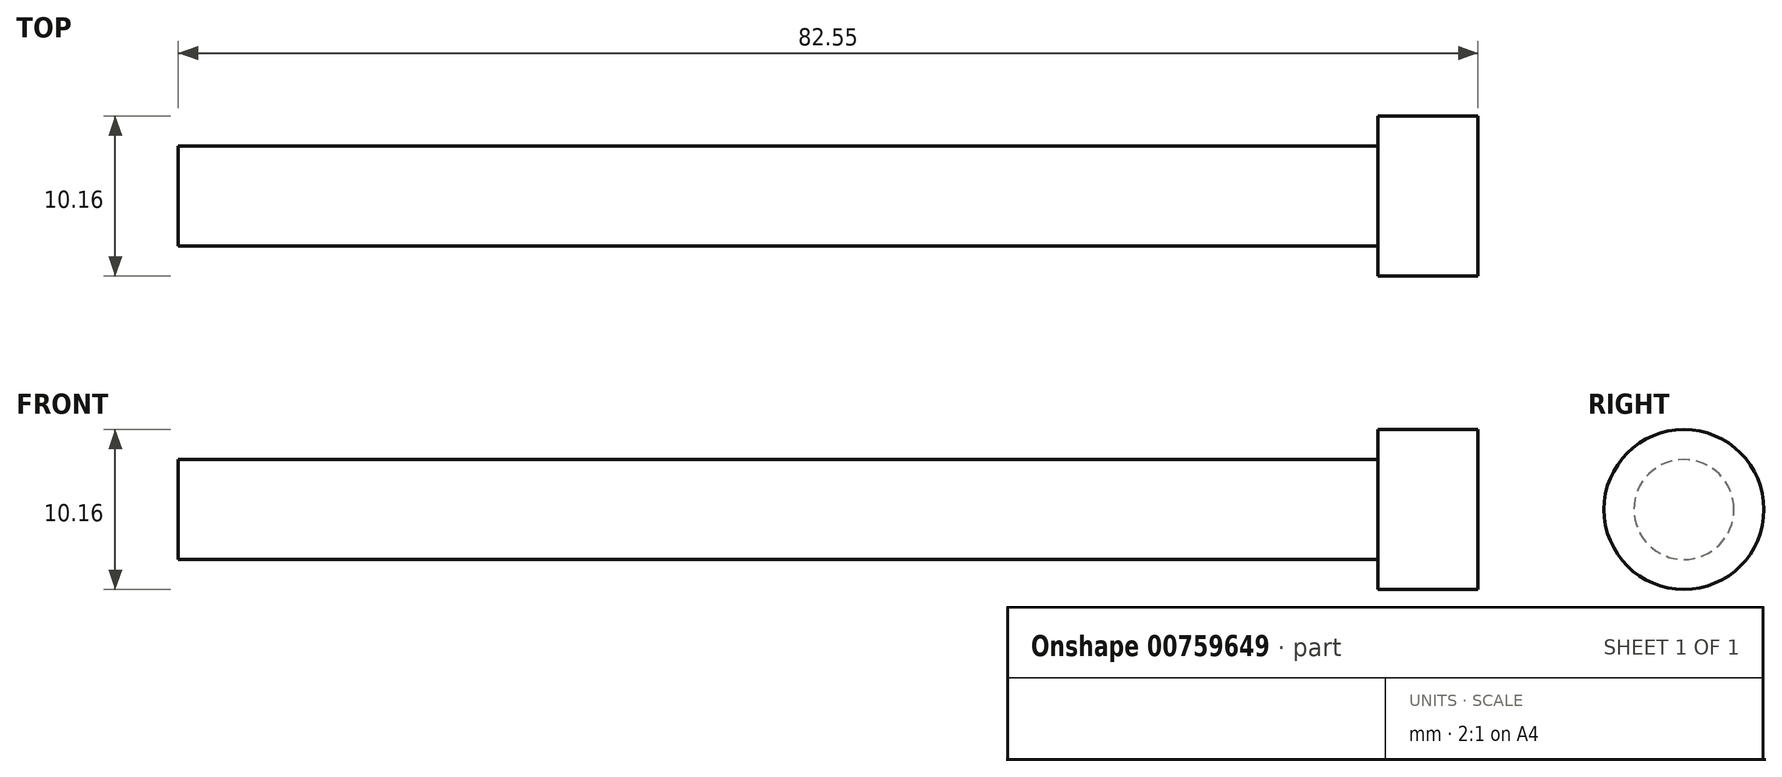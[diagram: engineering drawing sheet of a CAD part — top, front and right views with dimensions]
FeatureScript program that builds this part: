
annotation { "Feature Type Name" : "Feature", "Feature Type Description" : "" }
export const myFeature = defineFeature(function(context is Context, id is Id, definition is map)
    precondition{}
    {
        {
            var Q0;
            Q0=qCreatedBy(makeId("Right.planeOp"),FACE);
            var sketch = newSketch(context, id + "F0", { "sketchPlane" : qUnion([Q0])});
            skCircle(sketch, "E0", {"center": v(0, 0) * mm, "radius": 3.18 * mm});
            skSolve(sketch);
        }
        {
            var Q0;
            Q0=makeQuery(id+"F0.imprint","IMPRINT",FACE,{"disambiguationData":[TD([[makeQuery(id+"F0.imprint","IMPRINT",EDGE,{"derivedFrom":sQuery(id+"F0.wireOp",EDGE,"E0")}),1.0]])]});
            extrude(context, id + "F1", {"entities" : qUnion([Q0]), "depth" : 76.2 * mm, "offsetDistance" : 25.4 * mm, "symmetric" : true});
        }
        {
            var Q0;
            Q0=makeQuery(id+"F1.opExtrude","CAP_FACE",FACE,{"disambiguationData":[OSD([sQuery(id+"F0.wireOp",EDGE,"E0")])],"isStart":false});
            var sketch = newSketch(context, id + "F2", { "sketchPlane" : qUnion([Q0])});
            skCircle(sketch, "E1", {"center": v(0, 0) * mm, "radius": 5.08 * mm});
            skSolve(sketch);
        }
        {
            var Q0;
            Q0=makeQuery(id+"F2.imprint","IMPRINT",FACE,{"disambiguationData":[TD([[makeQuery(id+"F2.imprint","IMPRINT",EDGE,{"derivedFrom":sQuery(id+"F2.wireOp",EDGE,"E1")}),1.0]])]});
            var Q1;
            Q1=makeQuery(id+"F2.imprint","IMPRINT",FACE,{"disambiguationData":[TD([[makeQuery(id+"F2.imprint","IMPRINT",EDGE,{"derivedFrom":makeQuery(id+"F1.opExtrude","CAP_EDGE",EDGE,{"disambiguationData":[OSD([sQuery(id+"F0.wireOp",EDGE,"E0")])],"isStart":false})}),1.0]])]});
            extrude(context, id + "F3", {"entities" : qUnion([Q0, Q1]), "operationType" : NewBodyOperationType.ADD, "depth" : 6.35 * mm, "offsetDistance" : 25.4 * mm});
        }
    });
